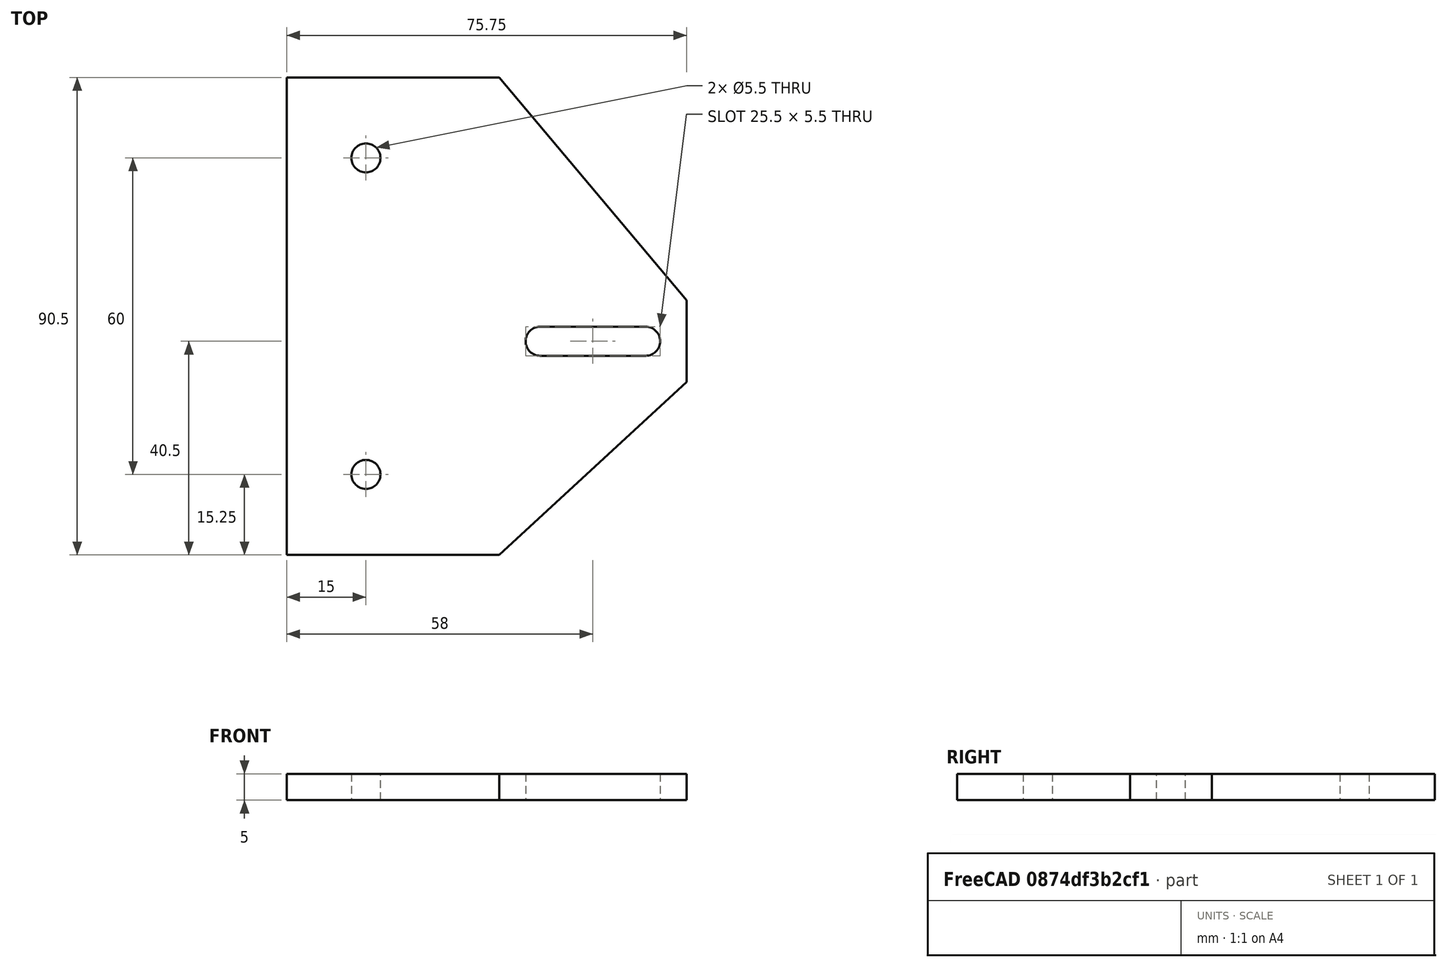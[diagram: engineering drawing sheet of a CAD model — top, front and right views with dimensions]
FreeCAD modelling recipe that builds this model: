
FCSTD DOCUMENT  (FreeCAD 0.19R)
Label: x-axis-pulley-mount
License: All rights reserved
LicenseURL: http://en.wikipedia.org/wiki/All_rights_reserved
objects: Sketcher::SketchObject×1, PartDesign::Pad×1, PartDesign::Body×1
note: 4 computed .brp shape members not serialized (recipe doc carries the construction recipe); baked Part::Feature solids carry a one-line shape summary decoded from their .brp

FEATURE [Sketcher::SketchObject] Sketch
  FullyConstrained = true
  MapMode = 5
  Support = -> [XY_Plane]
  sketch-geometry (24):
    g0: LineSegment StartX=0 StartY=0 StartZ=0 EndX=40.25 EndY=0 EndZ=0
    g1: LineSegment StartX=40.25 StartY=90.5 StartZ=0 EndX=0 EndY=90.5 EndZ=0
    g2: LineSegment StartX=0 StartY=90.5 StartZ=0 EndX=0 EndY=0 EndZ=0
    g3: LineSegment StartX=75.75 StartY=48.25 StartZ=0 EndX=75.75 EndY=32.75 EndZ=0
    g4: LineSegment StartX=40.25 StartY=90.5 StartZ=0 EndX=75.75 EndY=48.25 EndZ=0
    g5: LineSegment StartX=40.25 StartY=0 StartZ=0 EndX=75.75 EndY=32.75 EndZ=0
    g6: LineSegment StartX=15 StartY=90.5 StartZ=0 EndX=15 EndY=0 EndZ=0
    g7: Circle CenterX=15 CenterY=75.25 CenterZ=0 NormalX=0 NormalY=0 NormalZ=1 AngleXU=0 Radius=2.75
    g8: Circle CenterX=15 CenterY=15.25 CenterZ=0 NormalX=0 NormalY=0 NormalZ=1 AngleXU=0 Radius=2.75
    g9: LineSegment StartX=40.25 StartY=90.5 StartZ=0 EndX=40.25 EndY=0 EndZ=0
    g10: LineSegment StartX=48 StartY=43.25 StartZ=0 EndX=68 EndY=43.25 EndZ=0
    g11: LineSegment StartX=68 StartY=43.25 StartZ=0 EndX=68 EndY=37.75 EndZ=0
    g12: LineSegment StartX=68 StartY=37.75 StartZ=0 EndX=48 EndY=37.75 EndZ=0
    g13: LineSegment StartX=48 StartY=37.75 StartZ=0 EndX=48 EndY=43.25 EndZ=0
    g14: ArcOfCircle CenterX=68 CenterY=40.5 CenterZ=0 NormalX=0 NormalY=0 NormalZ=1 AngleXU=0 Radius=2.75 StartAngle=4.71239 EndAngle=7.85398
    g15: ArcOfCircle CenterX=48 CenterY=40.5 CenterZ=0 NormalX=0 NormalY=0 NormalZ=1 AngleXU=0 Radius=2.75 StartAngle=1.5708 EndAngle=4.71239
    g16: LineSegment StartX=75.75 StartY=48.25 StartZ=0 EndX=40.25 EndY=48.25 EndZ=0
    g17: LineSegment StartX=40.25 StartY=48.25 StartZ=0 EndX=40.25 EndY=32.75 EndZ=0
    g18: LineSegment StartX=40.25 StartY=32.75 StartZ=0 EndX=75.75 EndY=32.75 EndZ=0
    g19: GeomPoint X=70.75 Y=40.5 Z=0
    g20: GeomPoint X=45.25 Y=40.5 Z=0
    g21: GeomPoint X=40.25 Y=40.5 Z=0
    g22: LineSegment StartX=0 StartY=45.25 StartZ=0 EndX=40.25 EndY=45.25 EndZ=0
    g23: LineSegment StartX=40.25 StartY=40.5 StartZ=0 EndX=75.75 EndY=40.5 EndZ=0
  constraints (66):
    c: Coincident(g1,g2)
    c: Coincident(g2,g0)
    c: Horizontal(g0)
    c: Horizontal(g1)
    c: Vertical(g2)
    c: Coincident(g0,g-1)
    c: DistanceY(g2,g2) = 90.5
    c: Vertical(g3)
    c: Coincident(g4,g1)
    c: Coincident(g4,g3)
    c: Coincident(g5,g0)
    c: Coincident(g5,g3)
    c: DistanceX(g1,g1) = 40.25
    c: Equal(g1,g0)
    c: PointOnObject(g6,g1)
    c: PointOnObject(g6,g0)
    c: Vertical(g6)
    c: DistanceX(g1,g6) = 15
    c: PointOnObject(g7,g6)
    c: PointOnObject(g8,g6)
    c: DistanceY(g7,g6) = 15.25
    c: DistanceY(g6,g8) = 15.25
    c: Diameter(g8) = 5.5
    c: Diameter(g7) = 5.5
    c: Coincident(g9,g1)
    c: Coincident(g9,g0)
    c: Coincident(g10,g11)
    c: Coincident(g11,g12)
    c: Coincident(g12,g13)
    c: Coincident(g13,g10)
    c: Horizontal(g10)
    c: Horizontal(g12)
    c: Vertical(g11)
    c: Vertical(g13)
    c: PointOnObject(g14,g11)
    c: Coincident(g14,g10)
    c: Coincident(g14,g11)
    c: PointOnObject(g15,g13)
    c: Coincident(g15,g10)
    c: Coincident(g15,g12)
    c: Diameter(g15) = 5.5
    c: DistanceX(g10,g10) = 20
    c: Coincident(g16,g3)
    c: Horizontal(g16)
    c: Coincident(g17,g16)
    c: Vertical(g17)
    c: Coincident(g18,g17)
    c: Coincident(g18,g3)
    c: Horizontal(g18)
    c: PointOnObject(g19,g14)
    c: DistanceY(g10,g3) = 5
    c: PointOnObject(g20,g15)
    c: DistanceX(g16,g20) = 5
    c: PointOnObject(g21,g17)
    c: PointOnObject(g22,g9)
    c: Horizontal(g22)
    c: Symmetric(g1,g0,g22)
    c: Coincident(g23,g21)
    c: Horizontal(g23)
    c: Symmetric(g3,g3,g23)
    c: PointOnObject(g14,g23)
    c: PointOnObject(g20,g23)
    c: PointOnObject(g19,g23)
    c: DistanceX(g19,g3) = 5
    c: DistanceY(g21,g22) = 4.75
    c: PointOnObject(g16,g9)
FEATURE [PartDesign::Pad] Pad
  Direction = (1,1,1)
  Length = 5
  Length2 = 100
  Profile = -> Sketch
  Type = 0
FEATURE [PartDesign::Body] Body
  Group = -> [Sketch,Pad]
  Origin = -> Origin
  Tip = -> Pad
